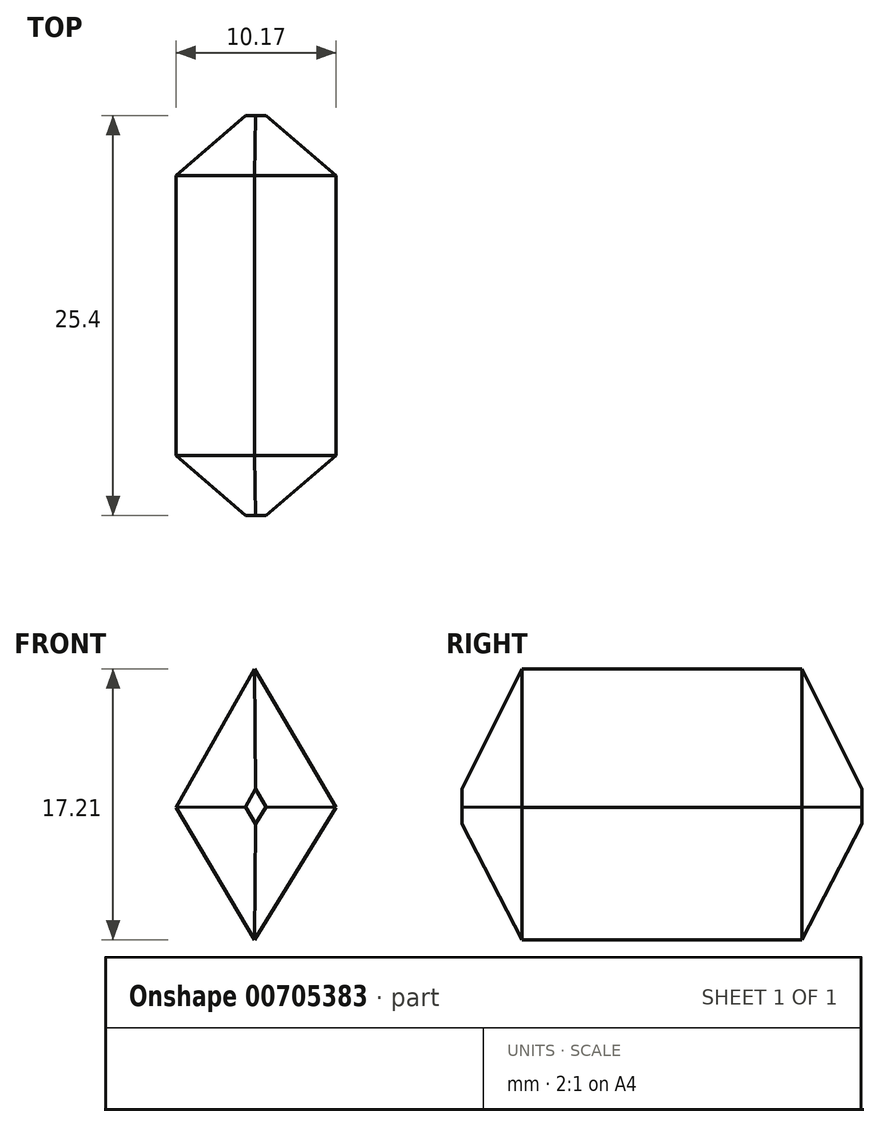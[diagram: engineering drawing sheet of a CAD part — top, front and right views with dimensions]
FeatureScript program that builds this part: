
annotation { "Feature Type Name" : "Feature", "Feature Type Description" : "" }
export const myFeature = defineFeature(function(context is Context, id is Id, definition is map)
    precondition{}
    {
        {
            var Q0;
            Q0=qCreatedBy(makeId("Front.planeOp"),FACE);
            var sketch = newSketch(context, id + "F0", { "sketchPlane" : qUnion([Q0])});
            skLineSegment(sketch, "E0", {"start": v(0, -14.96) * mm, "end": v(-8.84, 0) * mm});
            skLineSegment(sketch, "E1", {"start": v(-8.84, 0.14) * mm, "end": v(0, 15.35) * mm});
            skLineSegment(sketch, "E2", {"start": v(0, 15.35) * mm, "end": v(8.6, 0) * mm});
            skLineSegment(sketch, "E3", {"start": v(8.6, 0) * mm, "end": v(0, -14.96) * mm});
            skLineSegment(sketch, "E4", {"start": v(0, -8.41) * mm, "end": v(-4.97, 0) * mm});
            skLineSegment(sketch, "E5", {"start": v(-4.97, 0) * mm, "end": v(0, 8.8) * mm});
            skLineSegment(sketch, "E6", {"start": v(0, 8.8) * mm, "end": v(5.2, 0) * mm});
            skLineSegment(sketch, "E7", {"start": v(5.2, 0) * mm, "end": v(0, -8.41) * mm});
            skSolve(sketch);
        }
        {
            var Q0;
            Q0=makeQuery(id+"F0.imprint","IMPRINT",FACE,{"disambiguationData":[TD([[makeQuery(id+"F0.imprint","IMPRINT",EDGE,{"derivedFrom":sQuery(id+"F0.wireOp",EDGE,"E4")}),-1.0]])]});
            extrude(context, id + "F1", {"entities" : qUnion([Q0]), "depth" : 12.7 * mm, "offsetDistance" : 25.4 * mm});
        }
        {
            var Q0;
            Q0=makeQuery(id+"F1.opExtrude","CAP_FACE",FACE,{"disambiguationData":[OSD([sQuery(id+"F0.wireOp",EDGE,"E4"),sQuery(id+"F0.wireOp",EDGE,"E5"),sQuery(id+"F0.wireOp",EDGE,"E6"),sQuery(id+"F0.wireOp",EDGE,"E7")])],"isStart":true});
            extrude(context, id + "F2", {"entities" : qUnion([Q0]), "operationType" : NewBodyOperationType.ADD, "depth" : 12.7 * mm, "offsetDistance" : 25.4 * mm});
        }
        {
            var Q0;
            Q0=makeQuery(id+"F2.opExtrude","CAP_FACE",FACE,{"disambiguationData":[OSD([sQuery(id+"F0.wireOp",EDGE,"E4"),sQuery(id+"F0.wireOp",EDGE,"E5"),sQuery(id+"F0.wireOp",EDGE,"E6"),sQuery(id+"F0.wireOp",EDGE,"E7")])],"isStart":false});
            var Q1;
            Q1=makeQuery(id+"F1.opExtrude","CAP_FACE",FACE,{"disambiguationData":[OSD([sQuery(id+"F0.wireOp",EDGE,"E4"),sQuery(id+"F0.wireOp",EDGE,"E5"),sQuery(id+"F0.wireOp",EDGE,"E6"),sQuery(id+"F0.wireOp",EDGE,"E7")])],"isStart":false});
            chamfer(context, id + "F3", {"entities" : qUnion([Q0, Q1]), "width" : 3.8 * mm, "tangentPropagation" : true});
        }
    });
